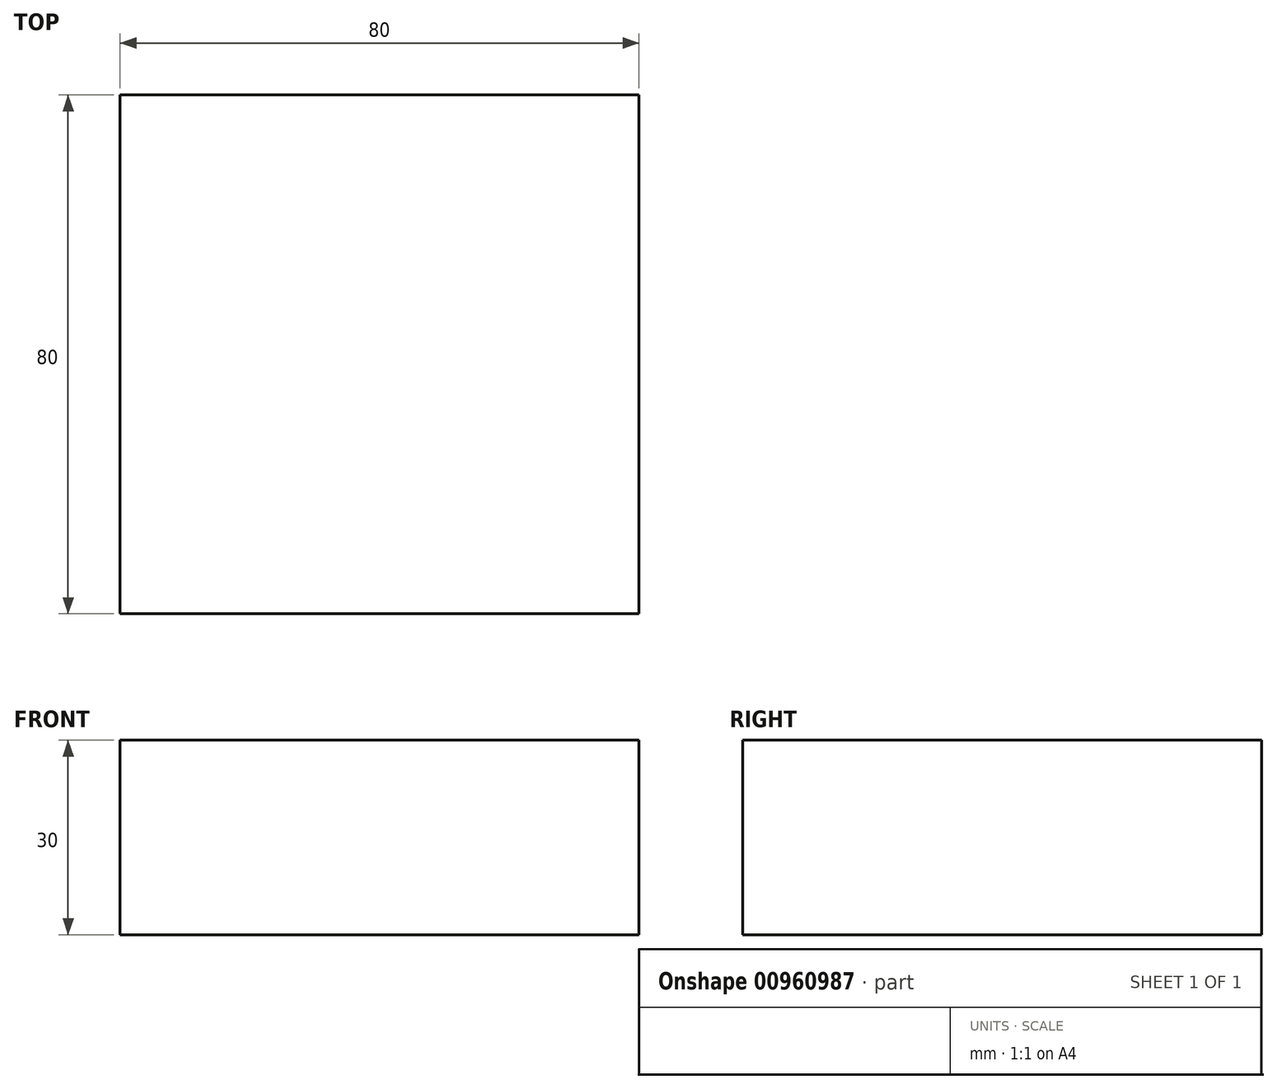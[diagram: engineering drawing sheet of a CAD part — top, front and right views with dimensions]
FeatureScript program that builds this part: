
annotation { "Feature Type Name" : "Feature", "Feature Type Description" : "" }
export const myFeature = defineFeature(function(context is Context, id is Id, definition is map)
    precondition{}
    {
        {
            var Q0;
            Q0=qCreatedBy(makeId("Front.planeOp"),FACE);
            var sketch = newSketch(context, id + "F0", { "sketchPlane" : qUnion([Q0])});
            skLineSegment(sketch, "E0.bottom", {"start": v(0, 0) * mm, "end": v(80, 0) * mm});
            skLineSegment(sketch, "E0.top", {"start": v(0, 30) * mm, "end": v(80, 30) * mm});
            skLineSegment(sketch, "E0.left", {"start": v(0, 0) * mm, "end": v(0, 30) * mm});
            skLineSegment(sketch, "E0.right", {"start": v(80, 0) * mm, "end": v(80, 30) * mm});
            skSolve(sketch);
        }
        {
            var Q0;
            Q0 = qSketchRegion(id + "F0", true);
            extrude(context, id + "F1", {"entities" : qUnion([Q0]), "depth" : 80 * mm, "offsetDistance" : 25 * mm});
        }
    });
